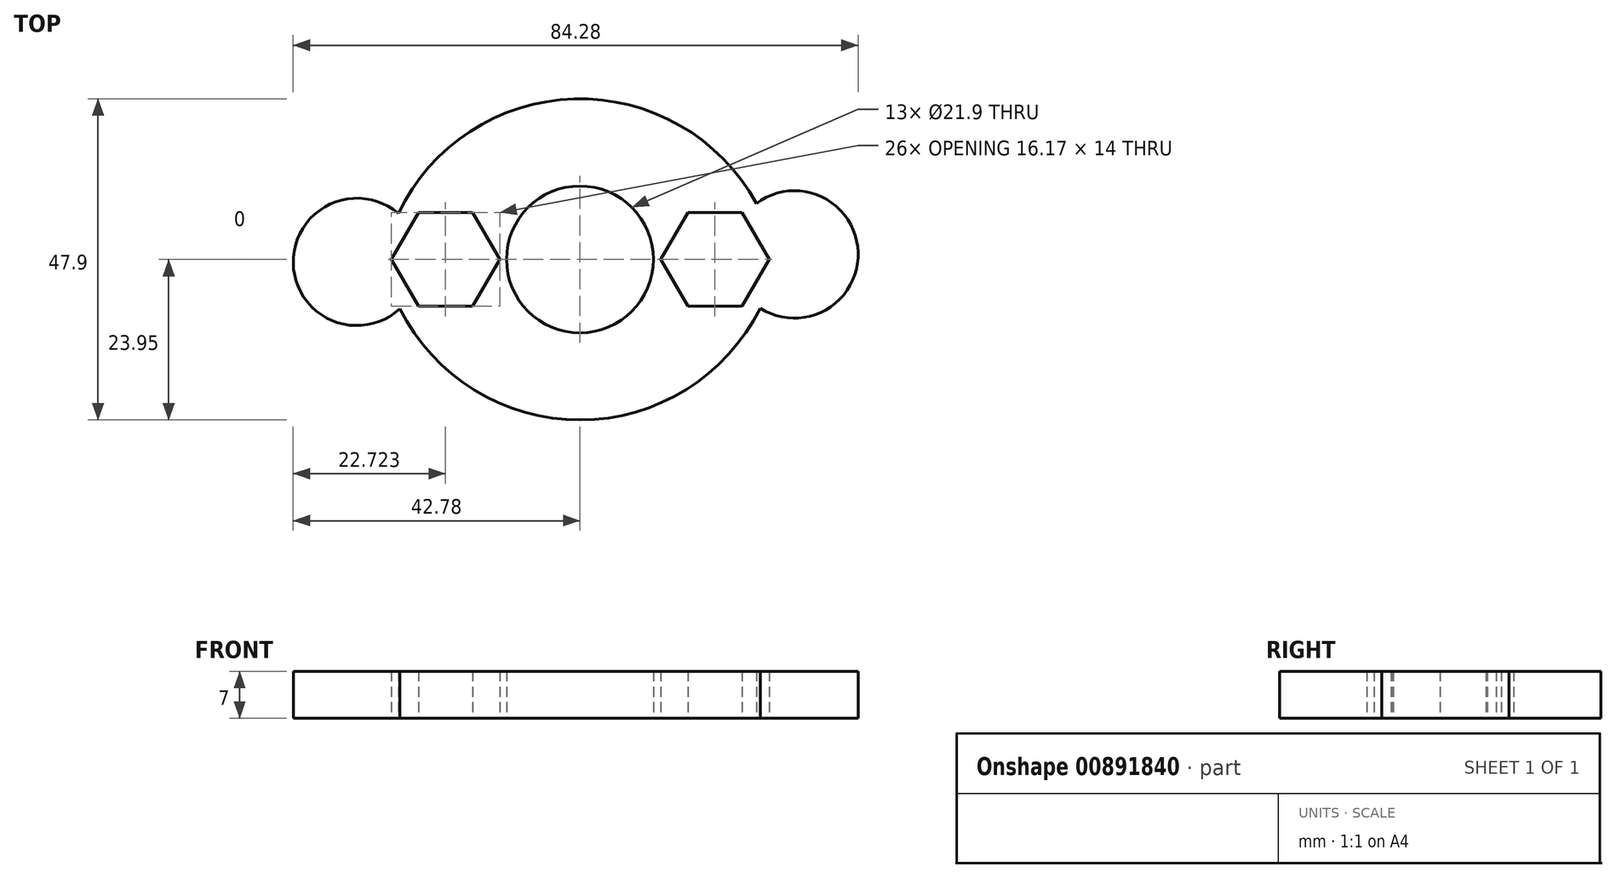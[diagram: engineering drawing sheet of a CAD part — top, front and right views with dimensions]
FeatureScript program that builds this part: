
annotation { "Feature Type Name" : "Feature", "Feature Type Description" : "" }
export const myFeature = defineFeature(function(context is Context, id is Id, definition is map)
    precondition{}
    {
        {
            var Q0;
            Q0=qCreatedBy(makeId("Top.planeOp"),FACE);
            var sketch = newSketch(context, id + "F0", { "sketchPlane" : qUnion([Q0])});
            skCircle(sketch, "E0", {"center": v(0, 0) * mm, "radius": 10.95 * mm});
            skArc(sketch, "E1", {"start": v(29.38, 0) * mm, "mid": v(0, 23.95) * mm, "end": v(-29.38, 0) * mm});
            skArc(sketch, "E2", {"start": v(-29.38, 0) * mm, "mid": v(0, -23.95) * mm, "end": v(29.38, 0) * mm});
            skCircle(sketch, "E3.cCircle", {"center": v(-20.06, 0) * mm, "radius": 7 * mm, "construction": true});
            skLineSegment(sketch, "E3.0", {"start": v(-24.1, 7) * mm, "end": v(-16.02, 7) * mm});
            skLineSegment(sketch, "E3.1", {"start": v(-16.02, 7) * mm, "end": v(-11.97, 0) * mm});
            skLineSegment(sketch, "E3.2", {"start": v(-11.97, 0) * mm, "end": v(-16.02, -7) * mm});
            skLineSegment(sketch, "E3.3", {"start": v(-16.02, -7) * mm, "end": v(-24.1, -7) * mm});
            skLineSegment(sketch, "E3.4", {"start": v(-24.1, -7) * mm, "end": v(-28.14, 0) * mm});
            skLineSegment(sketch, "E3.5", {"start": v(-28.14, 0) * mm, "end": v(-24.1, 7) * mm});
            skPoint(sketch, "E3.0.midPoint", {"position": v(-20.06, 7) * mm});
            skCircle(sketch, "E4.cCircle", {"center": v(20.14, 0) * mm, "radius": 7 * mm, "construction": true});
            skLineSegment(sketch, "E4.0", {"start": v(24.18, -7) * mm, "end": v(16.1, -7) * mm});
            skLineSegment(sketch, "E4.1", {"start": v(16.1, -7) * mm, "end": v(12.05, 0) * mm});
            skLineSegment(sketch, "E4.2", {"start": v(12.05, 0) * mm, "end": v(16.1, 7) * mm});
            skLineSegment(sketch, "E4.3", {"start": v(16.1, 7) * mm, "end": v(24.18, 7) * mm});
            skLineSegment(sketch, "E4.4", {"start": v(24.18, 7) * mm, "end": v(28.22, 0) * mm});
            skLineSegment(sketch, "E4.5", {"start": v(28.22, 0) * mm, "end": v(24.18, -7) * mm});
            skPoint(sketch, "E4.0.midPoint", {"position": v(20.14, -7) * mm});
            skArc(sketch, "E5", {"start": v(-27.1, 6.84) * mm, "mid": v(-42.78, -0.53) * mm, "end": v(-26.84, -7.35) * mm});
            skArc(sketch, "E6", {"start": v(26.89, -7.26) * mm, "mid": v(41.5, 1.09) * mm, "end": v(26.32, 8.35) * mm});
            skSolve(sketch);
        }
        {
            var Q0;
            Q0=makeQuery(id+"F0.imprint","IMPRINT",FACE,{"disambiguationData":[TD([[makeQuery(id+"F0.imprint","IMPRINT",EDGE,{"derivedFrom":sQuery(id+"F0.wireOp",EDGE,"E0")}),-1.0]])]});
            var Q1;
            {var subQ3=sQuery(id+"F0.wireOp",EDGE,"E5");Q1=makeQuery(id+"F0.imprint","IMPRINT",FACE,{"disambiguationData":[TD([[makeQuery(id+"F0.imprint","IMPRINT",EDGE,{"derivedFrom":subQ3}),1.0]])]});}
            var Q2;
            {var subQ3=sQuery(id+"F0.wireOp",EDGE,"E6");Q2=makeQuery(id+"F0.imprint","IMPRINT",FACE,{"disambiguationData":[TD([[makeQuery(id+"F0.imprint","IMPRINT",EDGE,{"derivedFrom":subQ3}),1.0]])]});}
            extrude(context, id + "F1", {"entities" : qUnion([Q0, Q1, Q2]), "depth" : 7 * mm, "offsetDistance" : 25 * mm});
        }
    });
